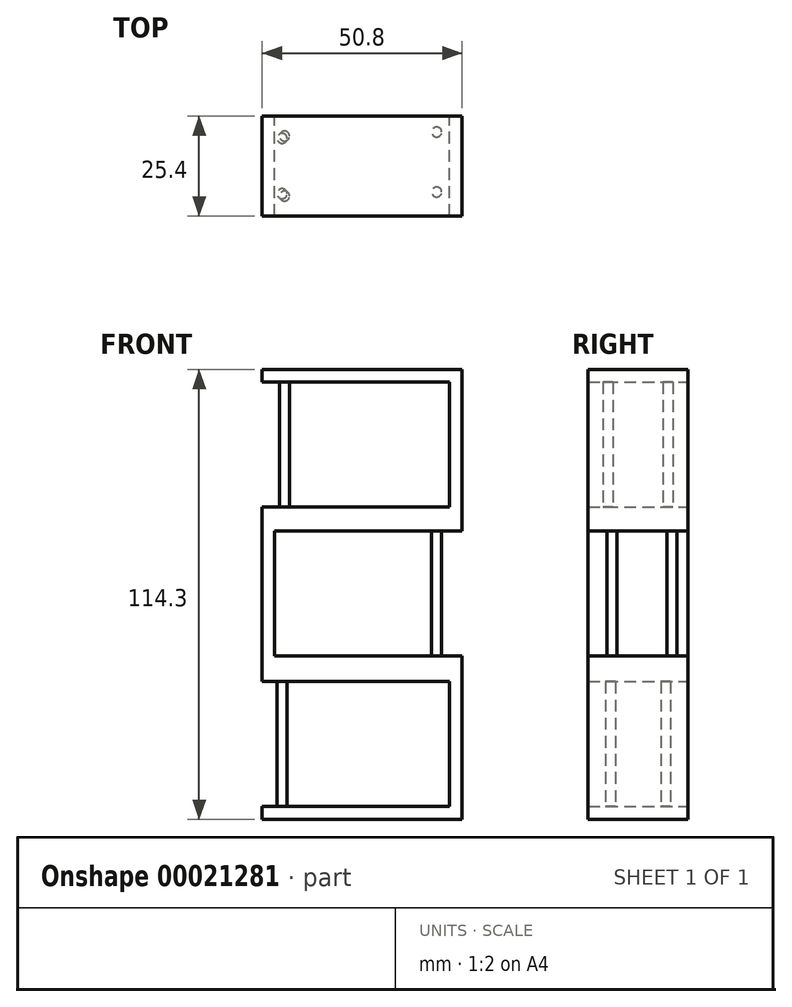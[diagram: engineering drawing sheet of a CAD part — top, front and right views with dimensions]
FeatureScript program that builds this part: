
annotation { "Feature Type Name" : "Feature", "Feature Type Description" : "" }
export const myFeature = defineFeature(function(context is Context, id is Id, definition is map)
    precondition{}
    {
        {
            var Q0;
            Q0=qCreatedBy(makeId("Front.planeOp"),FACE);
            var sketch = newSketch(context, id + "F0", { "sketchPlane" : qUnion([Q0])});
            skLineSegment(sketch, "E0.rect.bottom", {"start": v(-25.4, 57.15) * mm, "end": v(25.4, 57.15) * mm});
            skLineSegment(sketch, "E0.rect.top", {"start": v(-25.4, -57.15) * mm, "end": v(25.4, -57.15) * mm});
            skLineSegment(sketch, "E0.rect.left", {"start": v(-25.4, 57.15) * mm, "end": v(-25.4, -57.15) * mm});
            skLineSegment(sketch, "E0.rect.right", {"start": v(25.4, 57.15) * mm, "end": v(25.4, -57.15) * mm});
            skPoint(sketch, "E0.rect.middle", {"position": v(0, 0) * mm});
            skLineSegment(sketch, "E1.top", {"start": v(-25.4, 19.05) * mm, "end": v(25.4, 19.05) * mm});
            skLineSegment(sketch, "E1.left", {"start": v(-25.4, 57.15) * mm, "end": v(-25.4, 19.05) * mm});
            skLineSegment(sketch, "E1.right", {"start": v(25.4, 57.15) * mm, "end": v(25.4, 19.05) * mm});
            skLineSegment(sketch, "E2.top", {"start": v(-25.4, -19.05) * mm, "end": v(25.4, -19.05) * mm});
            skLineSegment(sketch, "E2.left", {"start": v(-25.4, 19.05) * mm, "end": v(-25.4, -19.05) * mm});
            skLineSegment(sketch, "E2.right", {"start": v(25.4, 19.05) * mm, "end": v(25.4, -19.05) * mm});
            skLineSegment(sketch, "E3.rect.bottom", {"start": v(-22.22, 53.98) * mm, "end": v(22.23, 53.98) * mm});
            skLineSegment(sketch, "E3.rect.top", {"start": v(-22.22, 22.23) * mm, "end": v(22.23, 22.23) * mm});
            skLineSegment(sketch, "E3.rect.right", {"start": v(22.23, 53.98) * mm, "end": v(22.23, 22.23) * mm});
            skPoint(sketch, "E3.rect.middle", {"position": v(0, 38.1) * mm});
            skLineSegment(sketch, "E4.bottom", {"start": v(-25.4, 53.98) * mm, "end": v(22.23, 53.98) * mm});
            skLineSegment(sketch, "E4.top", {"start": v(-25.4, 22.23) * mm, "end": v(22.23, 22.23) * mm});
            skLineSegment(sketch, "E4.left", {"start": v(-25.4, 53.98) * mm, "end": v(-25.4, 22.23) * mm});
            skLineSegment(sketch, "E5.bottom", {"start": v(25.4, 16.1) * mm, "end": v(-22.22, 16.1) * mm});
            skLineSegment(sketch, "E5.top", {"start": v(25.4, -15.65) * mm, "end": v(-22.22, -15.65) * mm});
            skLineSegment(sketch, "E5.left", {"start": v(25.4, 16.1) * mm, "end": v(25.4, -15.65) * mm});
            skLineSegment(sketch, "E5.right", {"start": v(-22.22, 16.1) * mm, "end": v(-22.22, -15.65) * mm});
            skLineSegment(sketch, "E6.bottom", {"start": v(-25.4, -22.12) * mm, "end": v(22.23, -22.12) * mm});
            skLineSegment(sketch, "E6.top", {"start": v(-25.4, -53.87) * mm, "end": v(22.23, -53.87) * mm});
            skLineSegment(sketch, "E6.left", {"start": v(-25.4, -22.12) * mm, "end": v(-25.4, -53.87) * mm});
            skLineSegment(sketch, "E6.right", {"start": v(22.23, -22.12) * mm, "end": v(22.23, -53.87) * mm});
            skSolve(sketch);
        }
        {
            var Q0;
            {var subQ10=sQuery(id+"F0.wireOp",EDGE,"E0.rect.bottom");Q0=makeQuery(id+"F0.imprint","IMPRINT",FACE,{"disambiguationData":[TD([[makeQuery(id+"F0.imprint","IMPRINT",EDGE,{"derivedFrom":subQ10}),-1.0]])]});}
            var Q1;
            {var subQ5=sQuery(id+"F0.wireOp",EDGE,"E1.top");Q1=makeQuery(id+"F0.imprint","IMPRINT",FACE,{"disambiguationData":[TD([[makeQuery(id+"F0.imprint","IMPRINT",EDGE,{"derivedFrom":subQ5}),-1.0]])]});}
            var Q2;
            {var subQ5=sQuery(id+"F0.wireOp",EDGE,"E0.rect.top");Q2=makeQuery(id+"F0.imprint","IMPRINT",FACE,{"disambiguationData":[TD([[makeQuery(id+"F0.imprint","IMPRINT",EDGE,{"derivedFrom":subQ5}),1.0]])]});}
            extrude(context, id + "F1", {"entities" : qUnion([Q0, Q1, Q2]), "depth" : 25.4 * mm});
        }
        {
            var Q0;
            Q0=makeQuery(id+"F1.opExtrude","SWEPT_FACE",FACE,{"disambiguationData":[OSD([sQuery(id+"F0.wireOp",EDGE,"E4.top")])]});
            var sketch = newSketch(context, id + "F2", { "sketchPlane" : qUnion([Q0])});
            skCircle(sketch, "E7", {"center": v(-19.72, -5.08) * mm, "radius": 1.27 * mm});
            skCircle(sketch, "E8", {"center": v(-19.72, -20.32) * mm, "radius": 1.27 * mm});
            skSolve(sketch);
        }
        {
            var Q0;
            Q0 = qSketchRegion(id + "F2", true);
            extrude(context, id + "F3", {"entities" : qUnion([Q0]), "operationType" : NewBodyOperationType.ADD, "depth" : 33.98 * mm});
        }
        {
            var Q0;
            Q0=makeQuery(id+"F1.opExtrude","SWEPT_FACE",FACE,{"disambiguationData":[OSD([sQuery(id+"F0.wireOp",EDGE,"E5.top")])]});
            var sketch = newSketch(context, id + "F4", { "sketchPlane" : qUnion([Q0])});
            skCircle(sketch, "E9", {"center": v(18.94, -19.29) * mm, "radius": 1.27 * mm});
            skCircle(sketch, "E10", {"center": v(18.94, -4.05) * mm, "radius": 1.27 * mm});
            skSolve(sketch);
        }
        {
            var Q0;
            Q0 = qSketchRegion(id + "F4", true);
            extrude(context, id + "F5", {"entities" : qUnion([Q0]), "operationType" : NewBodyOperationType.ADD, "depth" : 32.13 * mm});
        }
        {
            var Q0;
            Q0=makeQuery(id+"F1.opExtrude","SWEPT_FACE",FACE,{"disambiguationData":[OSD([sQuery(id+"F0.wireOp",EDGE,"E6.top")])]});
            var sketch = newSketch(context, id + "F6", { "sketchPlane" : qUnion([Q0])});
            skCircle(sketch, "E11", {"center": v(-20.32, -5.68) * mm, "radius": 1.27 * mm});
            skCircle(sketch, "E12", {"center": v(-20.32, -19.72) * mm, "radius": 1.27 * mm});
            skSolve(sketch);
        }
        {
            var Q0;
            Q0 = qSketchRegion(id + "F6", true);
            extrude(context, id + "F7", {"entities" : qUnion([Q0]), "operationType" : NewBodyOperationType.ADD, "depth" : 33.1 * mm});
        }
    });
